# Revit family: ROSENBERG_MINIBEL_900_A
name_source: partatom
category: Wyposażenie mechaniczne
revit_build: Autodesk Revit MEP 2016 (Build: 20150220_1215(x64)
units: mm (PartAtom-declared; Revit-internal decimal feet)

## family parameters
Numer OmniClass = 23.75.00.00
Oparty na płaszczyźnie roboczej = Tak
Punkt obliczania pomieszczeń = Nie
Tnij formami wycięć po wczytaniu = Nie
Typ części = Normalny
Tytuł OmniClass = Climate Control (HVAC)
Współdzielony = Nie
Wymiar okrągłego złącza = Użyj średnicy
Zawsze pionowo = Tak

## types (1)
- MIN 900 A
    600 = Nie
    900 = Tak
    Częstotliwość pracy = 50 Hz
    Dane techniczne = https://rosenberg.pl
    Domyślna rzędna = 1219 mm
    Elewacja = 900 mm  [stored 2.95276 ft]
    Klasa szczelności = IP21
    Masa = 12.50 kg
    Materiał = MINIBEL obudowa
    Materiał 2 = MINIBEL obudowa 2
    Moc znamionowa = 90 W
    Model = MIN 900 A
    Napięcie znamionowe = 230 V
    Numer katalogowy = AIRCOR06015
    Opis = Kurtyna powietrzna MINIBEL
    Producent = Rosenberg
    Prąd znamionowy = 1 A
    URL = https://rosenberg.pl
    Wydajność = 630.0 m³/h
    Zasięg = do 1,8 m

note: [stored X ft] marks values corroborated as IEEE doubles in the binary element streams (Revit-internal decimal feet)

## geometry (parser evidence)
native form markers: Blend x4, Sweep x7
no freeform markers — native parametric forms only
